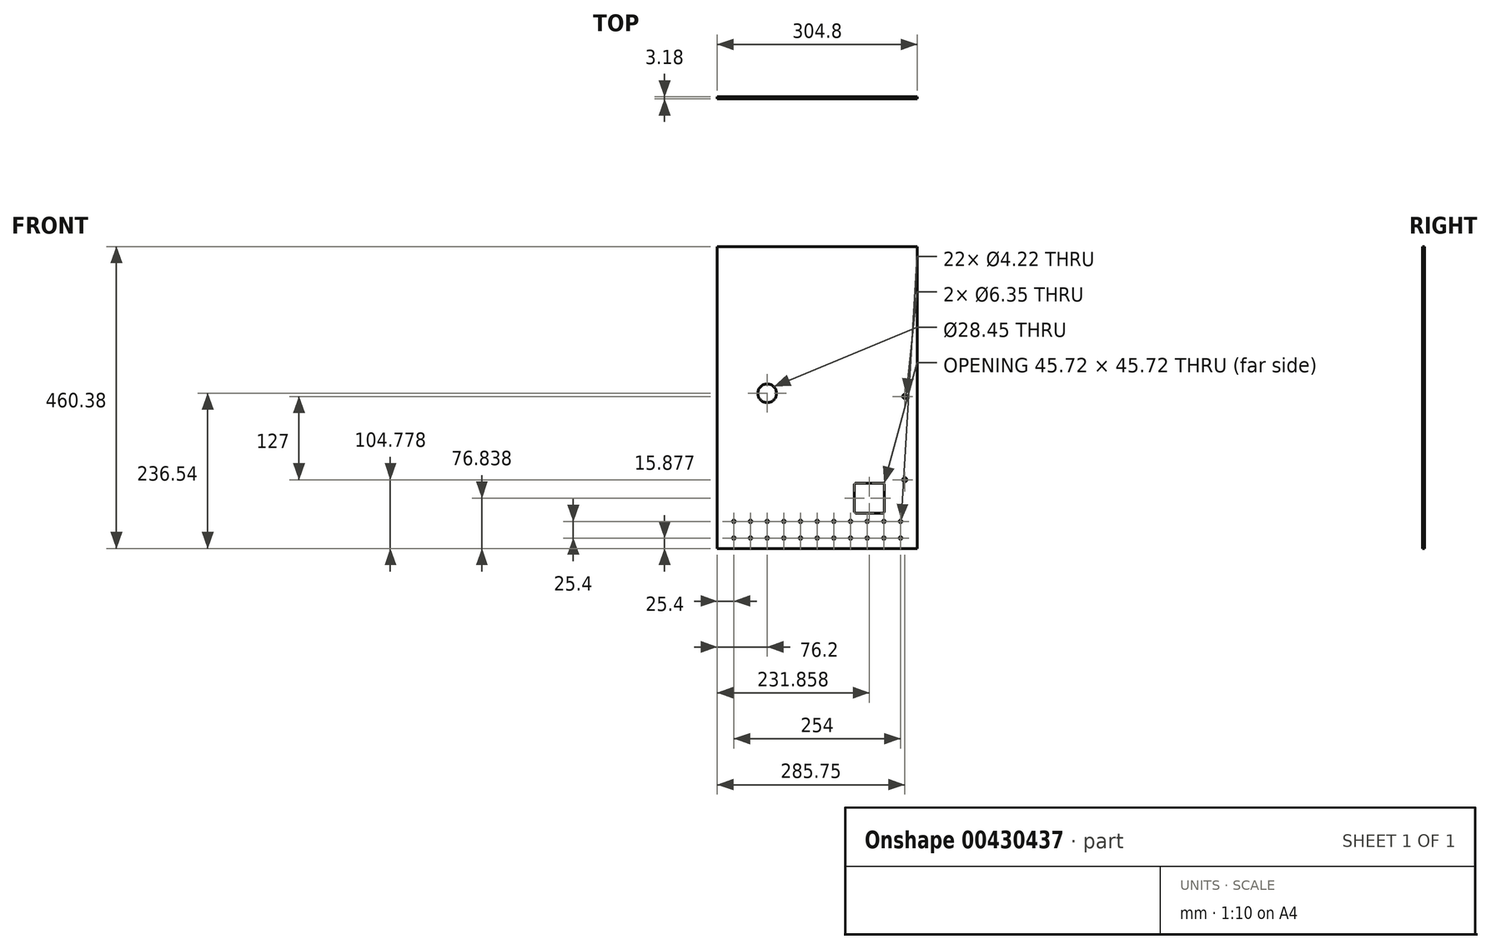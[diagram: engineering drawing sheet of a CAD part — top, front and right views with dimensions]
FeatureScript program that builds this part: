
annotation { "Feature Type Name" : "Feature", "Feature Type Description" : "" }
export const myFeature = defineFeature(function(context is Context, id is Id, definition is map)
    precondition{}
    {
        {
            var Q0;
            Q0=qCreatedBy(makeId("Front.planeOp"),FACE);
            var sketch = newSketch(context, id + "F0", { "sketchPlane" : qUnion([Q0])});
            skCircle(sketch, "E0", {"center": v(0, 0) * mm, "radius": 61.91 * mm, "construction": true});
            skArc(sketch, "E1", {"start": v(0, -182.56) * mm, "mid": v(140.87, -116.12) * mm, "end": v(179.2, 34.83) * mm, "construction": true});
            skLineSegment(sketch, "E2", {"start": v(0, -182.56) * mm, "end": v(132.8, -182.56) * mm, "construction": true});
            skLineSegment(sketch, "E3", {"start": v(228.6, -182.56) * mm, "end": v(228.6, 34.83) * mm, "construction": true});
            skLineSegment(sketch, "E4", {"start": v(228.6, 34.83) * mm, "end": v(179.2, 34.83) * mm, "construction": true});
            skLineSegment(sketch, "E5", {"start": v(0, 0) * mm, "end": v(182.56, 0) * mm, "construction": true});
            skLineSegment(sketch, "E6", {"start": v(0, 0) * mm, "end": v(179.2, 34.83) * mm, "construction": true});
            skLineSegment(sketch, "E7", {"start": v(209.55, -182.56) * mm, "end": v(209.55, 58.37) * mm, "construction": true});
            skCircle(sketch, "E8", {"center": v(209.55, -131.76) * mm, "radius": 3.17 * mm, "construction": true});
            skCircle(sketch, "E9", {"center": v(209.55, -4.76) * mm, "radius": 3.18 * mm, "construction": true});
            skLineSegment(sketch, "E10.top", {"start": v(178.52, -136.84) * mm, "end": v(132.8, -136.84) * mm});
            skLineSegment(sketch, "E10.left", {"start": v(178.52, -182.56) * mm, "end": v(178.52, -136.84) * mm});
            skLineSegment(sketch, "E10.right", {"start": v(132.8, -182.56) * mm, "end": v(132.8, -136.84) * mm});
            skPoint(sketch, "E10.middle", {"position": v(155.66, -159.7) * mm});
            skLineSegment(sketch, "E11.trimOffspring", {"start": v(178.52, -182.56) * mm, "end": v(228.6, -182.56) * mm, "construction": true});
            skSolve(sketch);
        }
        {
            var Q0;
            Q0=qCreatedBy(makeId("Front.planeOp"),FACE);
            var sketch = newSketch(context, id + "F1", { "sketchPlane" : qUnion([Q0])});
            skPoint(sketch, "E12.0", {"position": v(228.6, -182.56) * mm});
            skCircle(sketch, "E13.0", {"center": v(209.55, -131.76) * mm, "radius": 3.17 * mm});
            skCircle(sketch, "E14.0", {"center": v(209.55, -4.76) * mm, "radius": 3.18 * mm});
            skLineSegment(sketch, "E15.top", {"start": v(228.6, 223.84) * mm, "end": v(-76.2, 223.84) * mm});
            skLineSegment(sketch, "E15.left", {"start": v(228.6, -182.56) * mm, "end": v(228.6, 223.84) * mm});
            skLineSegment(sketch, "E15.right", {"start": v(-76.2, -182.56) * mm, "end": v(-76.2, 223.84) * mm});
            skLineSegment(sketch, "E16", {"start": v(228.6, -182.56) * mm, "end": v(178.52, -182.56) * mm});
            skCircle(sketch, "E17", {"center": v(0, 0) * mm, "radius": 14.22 * mm});
            skLineSegment(sketch, "E18.top", {"start": v(175.98, -136.84) * mm, "end": v(135.34, -136.84) * mm});
            skLineSegment(sketch, "E18.left", {"start": v(178.52, -180.02) * mm, "end": v(178.52, -139.38) * mm});
            skLineSegment(sketch, "E18.right", {"start": v(132.8, -180.02) * mm, "end": v(132.8, -139.38) * mm});
            skPoint(sketch, "E18.middle", {"position": v(155.66, -159.7) * mm});
            skLineSegment(sketch, "E19.trimOffspring", {"start": v(132.8, -182.56) * mm, "end": v(-76.2, -182.56) * mm});
            skPoint(sketch, "E20.visualSharp", {"position": v(178.52, -136.84) * mm});
            skArc(sketch, "E20.filletArc", {"start": v(178.52, -139.38) * mm, "mid": v(177.77, -137.59) * mm, "end": v(175.98, -136.84) * mm});
            skPoint(sketch, "E21.visualSharp", {"position": v(132.8, -136.84) * mm});
            skArc(sketch, "E21.filletArc", {"start": v(135.34, -136.84) * mm, "mid": v(133.54, -137.59) * mm, "end": v(132.8, -139.38) * mm});
            skPoint(sketch, "E22.visualSharp", {"position": v(132.8, -182.56) * mm});
            skPoint(sketch, "E23.visualSharp", {"position": v(178.52, -182.56) * mm});
            skLineSegment(sketch, "E24", {"start": v(-76.2, -182.56) * mm, "end": v(-76.2, -236.54) * mm});
            skLineSegment(sketch, "E25", {"start": v(-76.2, -236.54) * mm, "end": v(228.6, -236.54) * mm});
            skLineSegment(sketch, "E26", {"start": v(228.6, -236.54) * mm, "end": v(228.6, -182.56) * mm});
            skLineSegment(sketch, "E27", {"start": v(135.34, -182.56) * mm, "end": v(175.98, -182.56) * mm});
            skCircle(sketch, "E28", {"center": v(-50.8, -195.26) * mm, "radius": 2.1 * mm});
            skCircle(sketch, "E29", {"center": v(-50.8, -220.66) * mm, "radius": 2.1 * mm});
            skCircle(sketch, "E30.1.0.0", {"center": v(-25.4, -195.26) * mm, "radius": 2.1 * mm});
            skCircle(sketch, "E30.1.0.1", {"center": v(-25.4, -220.66) * mm, "radius": 2.1 * mm});
            skCircle(sketch, "E30.2.0.0", {"center": v(0, -195.26) * mm, "radius": 2.1 * mm});
            skCircle(sketch, "E30.2.0.1", {"center": v(0, -220.66) * mm, "radius": 2.1 * mm});
            skCircle(sketch, "E30.3.0.0", {"center": v(25.4, -195.26) * mm, "radius": 2.1 * mm});
            skCircle(sketch, "E30.3.0.1", {"center": v(25.4, -220.66) * mm, "radius": 2.1 * mm});
            skCircle(sketch, "E30.4.0.0", {"center": v(50.8, -195.26) * mm, "radius": 2.1 * mm});
            skCircle(sketch, "E30.4.0.1", {"center": v(50.8, -220.66) * mm, "radius": 2.1 * mm});
            skCircle(sketch, "E30.5.0.0", {"center": v(76.2, -195.26) * mm, "radius": 2.1 * mm});
            skCircle(sketch, "E30.5.0.1", {"center": v(76.2, -220.66) * mm, "radius": 2.1 * mm});
            skCircle(sketch, "E30.6.0.0", {"center": v(101.6, -195.26) * mm, "radius": 2.1 * mm});
            skCircle(sketch, "E30.6.0.1", {"center": v(101.6, -220.66) * mm, "radius": 2.1 * mm});
            skCircle(sketch, "E30.7.0.0", {"center": v(127, -195.26) * mm, "radius": 2.1 * mm});
            skCircle(sketch, "E30.7.0.1", {"center": v(127, -220.66) * mm, "radius": 2.1 * mm});
            skCircle(sketch, "E30.8.0.0", {"center": v(152.4, -195.26) * mm, "radius": 2.1 * mm});
            skCircle(sketch, "E30.8.0.1", {"center": v(152.4, -220.66) * mm, "radius": 2.1 * mm});
            skCircle(sketch, "E30.9.0.0", {"center": v(177.8, -195.26) * mm, "radius": 2.1 * mm});
            skCircle(sketch, "E30.9.0.1", {"center": v(177.8, -220.66) * mm, "radius": 2.1 * mm});
            skCircle(sketch, "E30.10.0.0", {"center": v(203.2, -195.26) * mm, "radius": 2.1 * mm});
            skCircle(sketch, "E30.10.0.1", {"center": v(203.2, -220.66) * mm, "radius": 2.1 * mm});
            skLineSegment(sketch, "E30.direction1", {"start": v(-50.8, -195.26) * mm, "end": v(-25.4, -195.26) * mm, "construction": true});
            skArc(sketch, "E31.filletArc", {"start": v(132.8, -180.02) * mm, "mid": v(133.54, -181.82) * mm, "end": v(135.34, -182.56) * mm});
            skArc(sketch, "E32.filletArc", {"start": v(175.98, -182.56) * mm, "mid": v(177.77, -181.82) * mm, "end": v(178.52, -180.02) * mm});
            skSolve(sketch);
        }
        {
            var Q0;
            Q0=makeQuery(id+"F1.imprint","IMPRINT",FACE,{"disambiguationData":[TD([[makeQuery(id+"F1.imprint","IMPRINT",EDGE,{"derivedFrom":sQuery(id+"F1.wireOp",EDGE,"E13.0")}),-1.0]])]});
            extrude(context, id + "F2", {"entities" : qUnion([Q0]), "depth" : 3.17 * mm});
        }
    });
